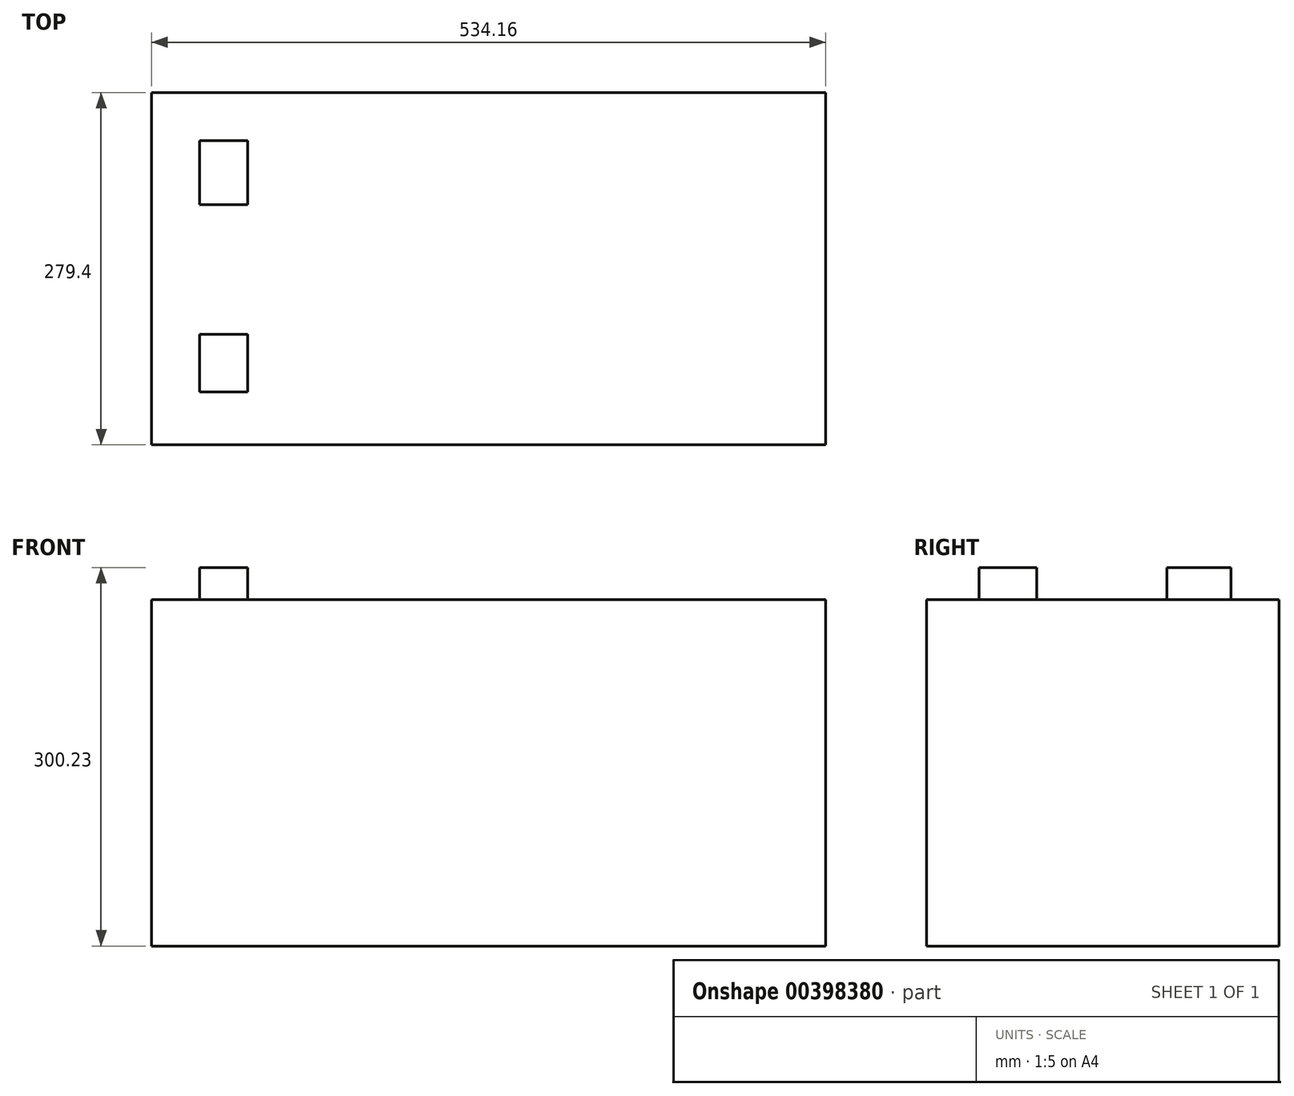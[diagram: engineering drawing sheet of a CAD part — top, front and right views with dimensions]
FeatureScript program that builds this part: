
annotation { "Feature Type Name" : "Feature", "Feature Type Description" : "" }
export const myFeature = defineFeature(function(context is Context, id is Id, definition is map)
    precondition{}
    {
        {
            var Q0;
            Q0=qCreatedBy(makeId("Top.planeOp"),FACE);
            var sketch = newSketch(context, id + "F0", { "sketchPlane" : qUnion([Q0])});
            skLineSegment(sketch, "E0.bottom", {"start": v(-267.08, -139.7) * mm, "end": v(267.08, -139.7) * mm});
            skLineSegment(sketch, "E0.top", {"start": v(-267.08, 139.7) * mm, "end": v(267.08, 139.7) * mm});
            skLineSegment(sketch, "E0.left", {"start": v(-267.08, -139.7) * mm, "end": v(-267.08, 139.7) * mm});
            skLineSegment(sketch, "E0.right", {"start": v(267.08, -139.7) * mm, "end": v(267.08, 139.7) * mm});
            skPoint(sketch, "E0.middle", {"position": v(0, 0) * mm});
            skSolve(sketch);
        }
        {
            var Q0;
            Q0 = qSketchRegion(id + "F0", true);
            extrude(context, id + "F1", {"entities" : qUnion([Q0]), "depth" : 274.83 * mm});
        }
        {
            var Q0;
            Q0=makeQuery(id+"F1.opExtrude","CAP_FACE",FACE,{"disambiguationData":[OSD([sQuery(id+"F0.wireOp",EDGE,"E0.bottom"),sQuery(id+"F0.wireOp",EDGE,"E0.top"),sQuery(id+"F0.wireOp",EDGE,"E0.left"),sQuery(id+"F0.wireOp",EDGE,"E0.right")])],"isStart":false});
            var sketch = newSketch(context, id + "F2", { "sketchPlane" : qUnion([Q0])});
            skLineSegment(sketch, "E1.bottom", {"start": v(-267.08, 139.7) * mm, "end": v(-228.98, 139.7) * mm});
            skLineSegment(sketch, "E1.left", {"start": v(-267.08, 139.7) * mm, "end": v(-267.08, 101.6) * mm});
            skLineSegment(sketch, "E2.bottom", {"start": v(-228.98, 101.6) * mm, "end": v(-190.88, 101.6) * mm});
            skLineSegment(sketch, "E2.top", {"start": v(-228.98, 50.8) * mm, "end": v(-190.88, 50.8) * mm});
            skLineSegment(sketch, "E2.left", {"start": v(-228.98, 101.6) * mm, "end": v(-228.98, 50.8) * mm});
            skLineSegment(sketch, "E3", {"start": v(-190.88, 50.8) * mm, "end": v(-190.88, 101.6) * mm});
            skLineSegment(sketch, "E4.top", {"start": v(-228.98, -97.96) * mm, "end": v(-190.88, -97.96) * mm});
            skLineSegment(sketch, "E4.right", {"start": v(-190.88, 101.6) * mm, "end": v(-190.88, 50.8) * mm});
            skLineSegment(sketch, "E5", {"start": v(-228.98, -52.17) * mm, "end": v(-190.88, -52.17) * mm});
            skLineSegment(sketch, "E6.trimOffspring", {"start": v(-228.98, -52.17) * mm, "end": v(-228.98, -97.96) * mm});
            skLineSegment(sketch, "E7.trimOffspring", {"start": v(-190.88, -52.17) * mm, "end": v(-190.88, -97.96) * mm});
            skSolve(sketch);
        }
        {
            var Q0;
            Q0 = qSketchRegion(id + "F2", true);
            extrude(context, id + "F3", {"entities" : qUnion([Q0]), "operationType" : NewBodyOperationType.ADD, "depth" : 25.4 * mm});
        }
    });
